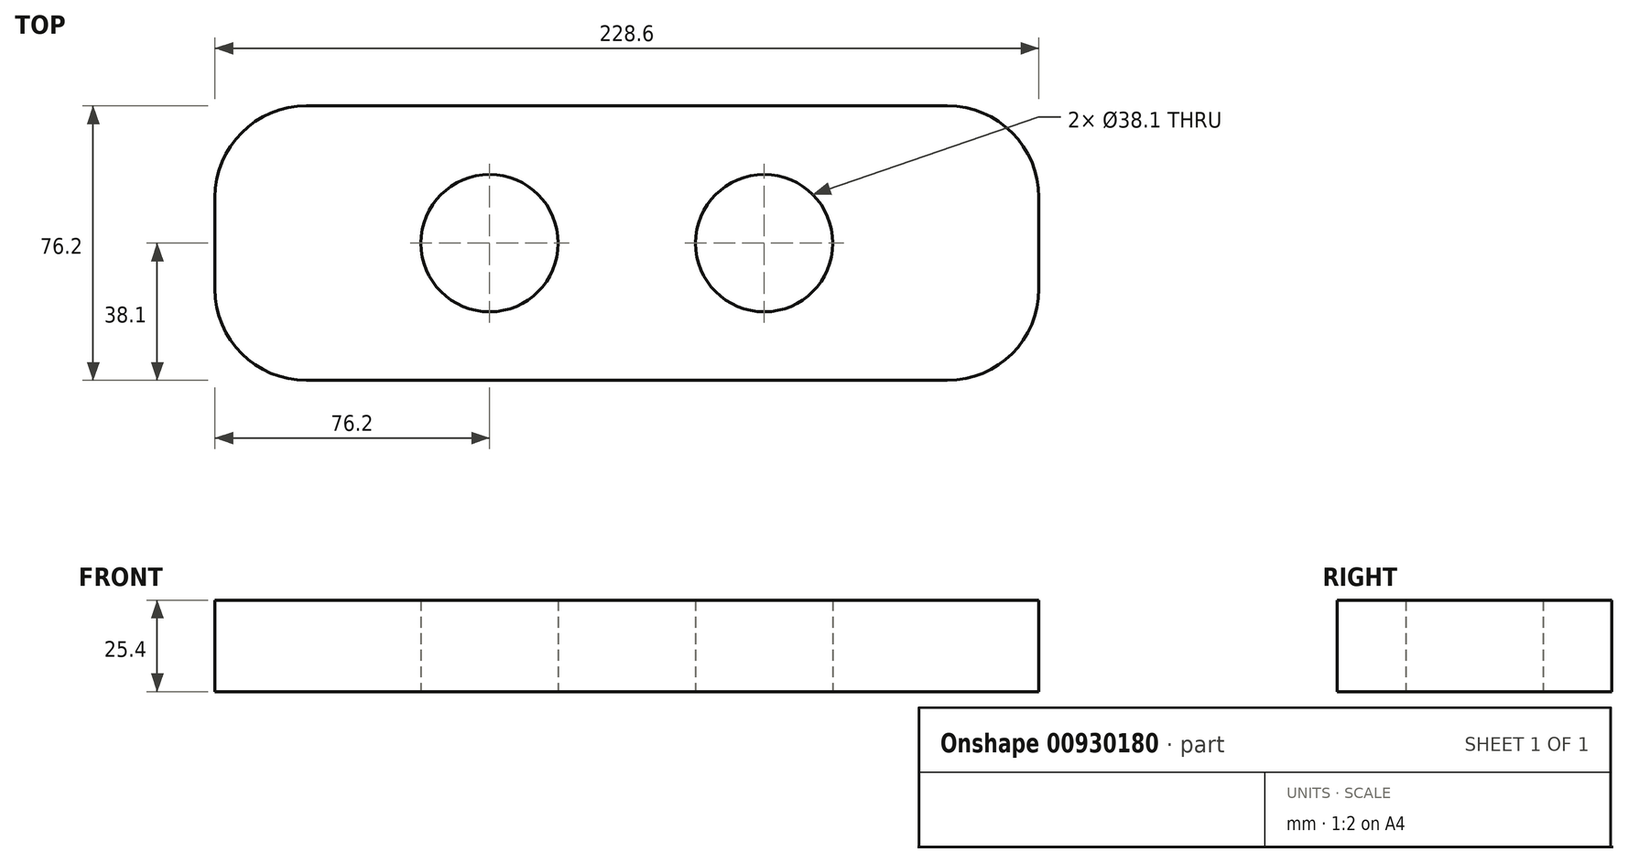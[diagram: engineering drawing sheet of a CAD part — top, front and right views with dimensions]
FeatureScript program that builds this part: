
annotation { "Feature Type Name" : "Feature", "Feature Type Description" : "" }
export const myFeature = defineFeature(function(context is Context, id is Id, definition is map)
    precondition{}
    {
        {
            var Q0;
            Q0=qCreatedBy(makeId("Top.planeOp"),FACE);
            var sketch = newSketch(context, id + "F0", { "sketchPlane" : qUnion([Q0])});
            skLineSegment(sketch, "E0.bottom", {"start": v(88.9, 38.1) * mm, "end": v(-88.9, 38.1) * mm});
            skLineSegment(sketch, "E0.top", {"start": v(88.9, -38.1) * mm, "end": v(-88.9, -38.1) * mm});
            skLineSegment(sketch, "E0.left", {"start": v(114.3, 12.7) * mm, "end": v(114.3, -12.7) * mm});
            skLineSegment(sketch, "E0.right", {"start": v(-114.3, 12.7) * mm, "end": v(-114.3, -12.7) * mm});
            skPoint(sketch, "E0.middle", {"position": v(0, 0) * mm});
            skLineSegment(sketch, "E1", {"start": v(-38.1, 38.1) * mm, "end": v(-38.1, -38.1) * mm, "construction": true});
            skLineSegment(sketch, "E2", {"start": v(38.1, 38.1) * mm, "end": v(38.1, -38.1) * mm, "construction": true});
            skLineSegment(sketch, "E3", {"start": v(-114.3, 0) * mm, "end": v(114.3, 0) * mm, "construction": true});
            skCircle(sketch, "E4", {"center": v(-38.1, 0) * mm, "radius": 19.05 * mm});
            skPoint(sketch, "E5", {"position": v(-38.1, 19.05) * mm});
            skCircle(sketch, "E6", {"center": v(38.1, 0) * mm, "radius": 19.05 * mm});
            skPoint(sketch, "E7", {"position": v(38.1, 19.05) * mm});
            skPoint(sketch, "E8.visualSharp", {"position": v(-114.3, 38.1) * mm});
            skArc(sketch, "E8.filletArc", {"start": v(-88.9, 38.1) * mm, "mid": v(-106.86, 30.66) * mm, "end": v(-114.3, 12.7) * mm});
            skPoint(sketch, "E9.visualSharp", {"position": v(-114.3, -38.1) * mm});
            skArc(sketch, "E9.filletArc", {"start": v(-114.3, -12.7) * mm, "mid": v(-106.86, -30.66) * mm, "end": v(-88.9, -38.1) * mm});
            skPoint(sketch, "E10.visualSharp", {"position": v(114.3, -38.1) * mm});
            skArc(sketch, "E10.filletArc", {"start": v(88.9, -38.1) * mm, "mid": v(106.86, -30.66) * mm, "end": v(114.3, -12.7) * mm});
            skPoint(sketch, "E11.visualSharp", {"position": v(114.3, 38.1) * mm});
            skArc(sketch, "E11.filletArc", {"start": v(114.3, 12.7) * mm, "mid": v(106.86, 30.66) * mm, "end": v(88.9, 38.1) * mm});
            skSolve(sketch);
        }
        {
            var Q0;
            Q0=qSketchRegion(id+"F0",true);
            extrude(context, id + "F1", {"entities" : qUnion([Q0]), "depth" : 25.4 * mm, "offsetDistance" : 25.4 * mm});
        }
    });
